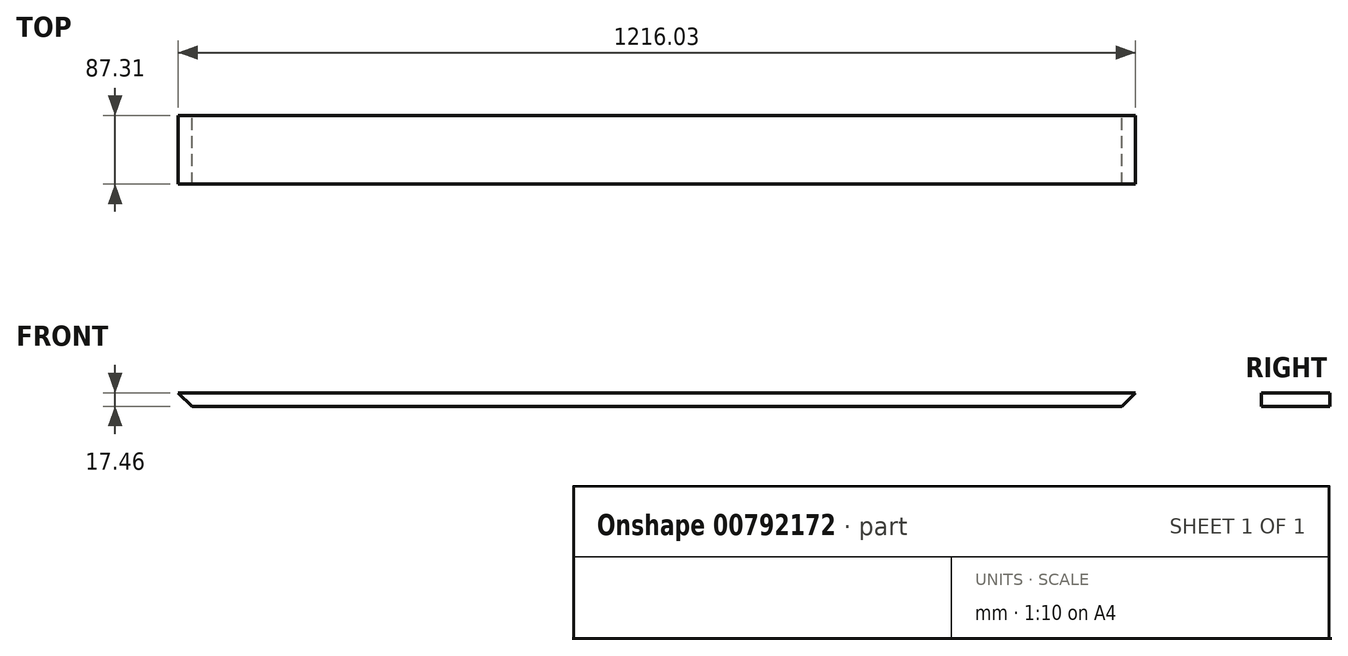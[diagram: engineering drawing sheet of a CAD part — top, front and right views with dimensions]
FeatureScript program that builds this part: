
annotation { "Feature Type Name" : "Feature", "Feature Type Description" : "" }
export const myFeature = defineFeature(function(context is Context, id is Id, definition is map)
    precondition{}
    {
        {
            var Q0;
            Q0=qCreatedBy(makeId("Top.planeOp"),FACE);
            var sketch = newSketch(context, id + "F0", { "sketchPlane" : qUnion([Q0])});
            skLineSegment(sketch, "E0.bottom", {"start": v(0, 0) * mm, "end": v(-1216.03, 0) * mm});
            skLineSegment(sketch, "E0.top", {"start": v(0, -87.31) * mm, "end": v(-1216.03, -87.31) * mm});
            skLineSegment(sketch, "E0.left", {"start": v(0, 0) * mm, "end": v(0, -87.31) * mm});
            skLineSegment(sketch, "E0.right", {"start": v(-1216.03, 0) * mm, "end": v(-1216.03, -87.31) * mm});
            skSolve(sketch);
        }
        {
            var Q0;
            Q0 = qSketchRegion(id + "F0", true);
            extrude(context, id + "F1", {"entities" : qUnion([Q0]), "depth" : 17.46 * mm, "offsetDistance" : 25.4 * mm});
        }
        {
            var Q0;
            Q0=makeQuery(id+"F1.opExtrude","SWEPT_FACE",FACE,{"disambiguationData":[OSD([sQuery(id+"F0.wireOp",EDGE,"E0.bottom")])]});
            var sketch = newSketch(context, id + "F2", { "sketchPlane" : qUnion([Q0])});
            skLineSegment(sketch, "E1", {"start": v(0, 17.46) * mm, "end": v(0, 0) * mm});
            skLineSegment(sketch, "E2", {"start": v(0, 0) * mm, "end": v(17.46, 0) * mm});
            skLineSegment(sketch, "E3", {"start": v(17.46, 0) * mm, "end": v(0, 17.46) * mm});
            skLineSegment(sketch, "E4", {"start": v(1216.03, 17.46) * mm, "end": v(1216.03, 0) * mm});
            skLineSegment(sketch, "E5", {"start": v(1216.03, 0) * mm, "end": v(1198.56, 0) * mm});
            skLineSegment(sketch, "E6", {"start": v(1198.56, 0) * mm, "end": v(1216.03, 17.46) * mm});
            skSolve(sketch);
        }
        {
            var Q0;
            Q0 = qSketchRegion(id + "F2", true);
            extrude(context, id + "F3", {"entities" : qUnion([Q0]), "operationType" : NewBodyOperationType.REMOVE, "oppositeDirection" : true, "depth" : 87.31 * mm, "offsetDistance" : 25.4 * mm});
        }
    });
